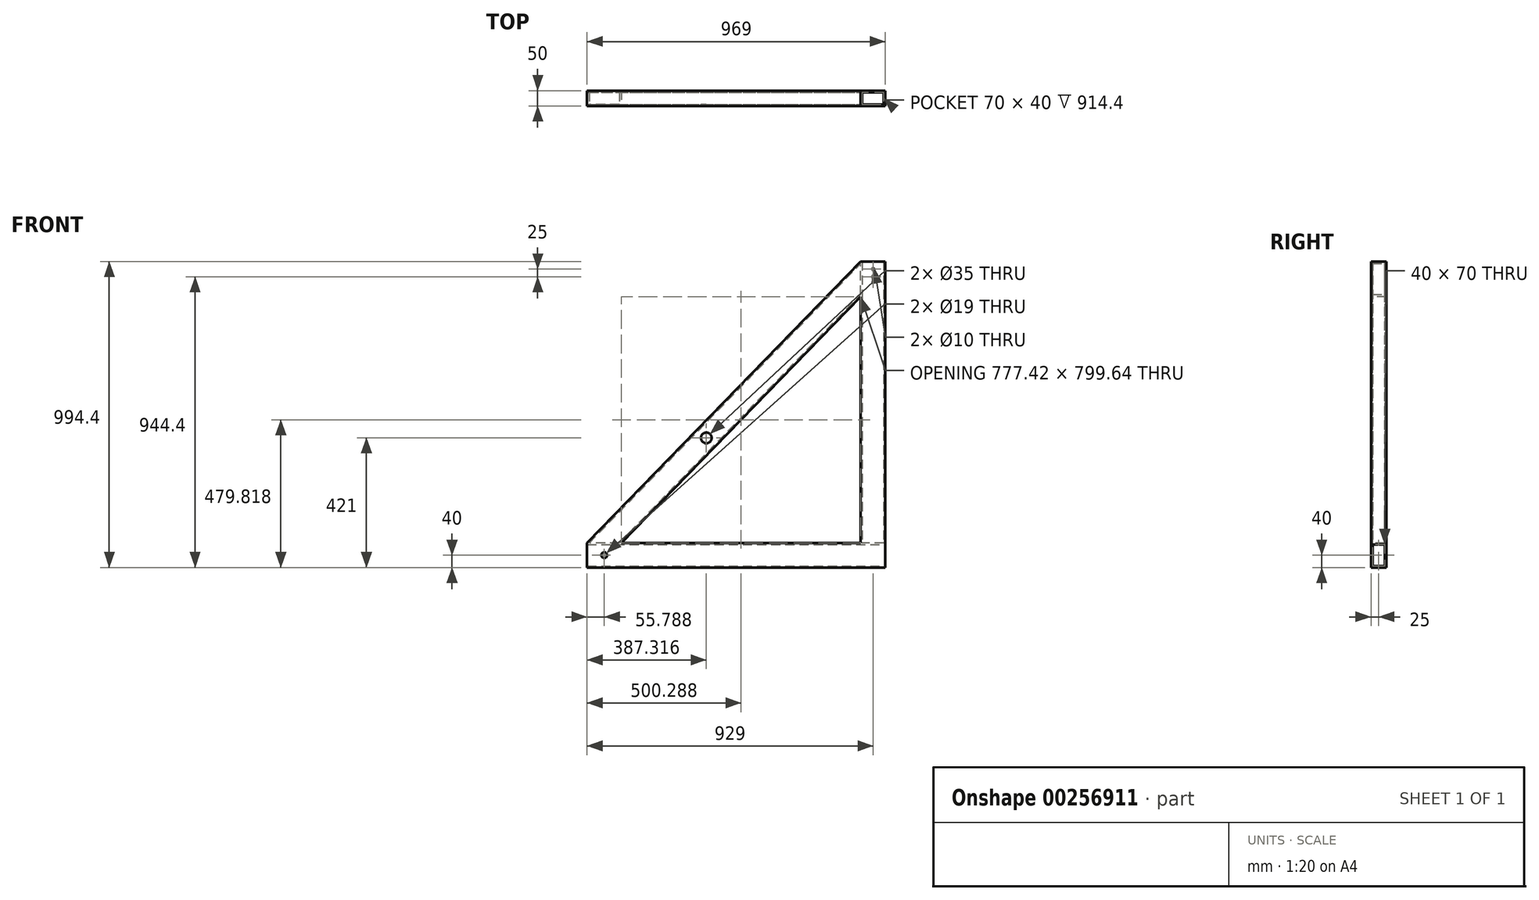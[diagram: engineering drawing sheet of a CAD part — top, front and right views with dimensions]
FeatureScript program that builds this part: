
annotation { "Feature Type Name" : "Feature", "Feature Type Description" : "" }
export const myFeature = defineFeature(function(context is Context, id is Id, definition is map)
    precondition{}
    {
        {
            var Q0;
            Q0=qCreatedBy(makeId("Right.planeOp"),FACE);
            var sketch = newSketch(context, id + "F0", { "sketchPlane" : qUnion([Q0])});
            skLineSegment(sketch, "E0.bottom", {"start": v(0, 0) * mm, "end": v(-50, 0) * mm});
            skLineSegment(sketch, "E0.top", {"start": v(0, 80) * mm, "end": v(-50, 80) * mm});
            skLineSegment(sketch, "E0.left", {"start": v(0, 0) * mm, "end": v(0, 80) * mm});
            skLineSegment(sketch, "E0.right", {"start": v(-50, 0) * mm, "end": v(-50, 80) * mm});
            skLineSegment(sketch, "E1.0", {"start": v(-5, 75) * mm, "end": v(-45, 75) * mm});
            skLineSegment(sketch, "E1.1", {"start": v(-5, 5) * mm, "end": v(-5, 75) * mm});
            skLineSegment(sketch, "E1.2", {"start": v(-5, 5) * mm, "end": v(-45, 5) * mm});
            skLineSegment(sketch, "E1.3", {"start": v(-45, 5) * mm, "end": v(-45, 75) * mm});
            skSolve(sketch);
        }
        {
            var Q0;
            Q0=makeQuery(id+"F0.imprint","IMPRINT",FACE,{"disambiguationData":[TD([[makeQuery(id+"F0.imprint","IMPRINT",EDGE,{"derivedFrom":sQuery(id+"F0.wireOp",EDGE,"E0.bottom")}),-1.0]])]});
            extrude(context, id + "F1", {"entities" : qUnion([Q0]), "oppositeDirection" : true, "depth" : 969 * mm});
        }
        {
            var Q0;
            Q0=makeQuery(id+"F1.opExtrude","SWEPT_FACE",FACE,{"disambiguationData":[OSD([sQuery(id+"F0.wireOp",EDGE,"E0.top")])]});
            var sketch = newSketch(context, id + "F2", { "sketchPlane" : qUnion([Q0])});
            skLineSegment(sketch, "E2.bottom", {"start": v(0, 0) * mm, "end": v(-80, 0) * mm});
            skLineSegment(sketch, "E2.top", {"start": v(0, -50) * mm, "end": v(-80, -50) * mm});
            skLineSegment(sketch, "E2.left", {"start": v(0, 0) * mm, "end": v(0, -50) * mm});
            skLineSegment(sketch, "E2.right", {"start": v(-80, 0) * mm, "end": v(-80, -50) * mm});
            skLineSegment(sketch, "E3.0", {"start": v(-5, -5) * mm, "end": v(-75, -5) * mm});
            skLineSegment(sketch, "E3.1", {"start": v(-5, -5) * mm, "end": v(-5, -45) * mm});
            skLineSegment(sketch, "E3.2", {"start": v(-5, -45) * mm, "end": v(-75, -45) * mm});
            skLineSegment(sketch, "E3.3", {"start": v(-75, -5) * mm, "end": v(-75, -45) * mm});
            skSolve(sketch);
        }
        {
            var Q0;
            Q0=makeQuery(id+"F2.imprint","IMPRINT",FACE,{"disambiguationData":[TD([[makeQuery(id+"F2.imprint","IMPRINT",EDGE,{"derivedFrom":sQuery(id+"F2.wireOp",EDGE,"E2.bottom")}),-1.0]])]});
            extrude(context, id + "F3", {"entities" : qUnion([Q0]), "operationType" : NewBodyOperationType.ADD, "depth" : 914.4 * mm});
        }
        {
            var Q0;
            Q0=makeQuery(id+"F3.boolean.opBoolean","MERGE",FACE,{"derivedFrom":[makeQuery(id+"F1.opExtrude","SWEPT_FACE",FACE,{"disambiguationData":[OSD([sQuery(id+"F0.wireOp",EDGE,"E0.right")])]}),makeQuery(id+"F3.opExtrude","SWEPT_FACE",FACE,{"disambiguationData":[OSD([sQuery(id+"F2.wireOp",EDGE,"E2.top")])]})]});
            var sketch = newSketch(context, id + "F4", { "sketchPlane" : qUnion([Q0])});
            skLineSegment(sketch, "E4", {"start": v(-969, 80) * mm, "end": v(-80, 994.4) * mm});
            skLineSegment(sketch, "E5.0", {"start": v(-857.42, 80) * mm, "end": v(-80, 879.64) * mm});
            skLineSegment(sketch, "E6", {"start": v(-80, 994.4) * mm, "end": v(-80, 879.64) * mm});
            skLineSegment(sketch, "E7", {"start": v(-969, 80) * mm, "end": v(-857.42, 80) * mm});
            skSolve(sketch);
        }
        {
            var Q0;
            Q0=makeQuery(id+"F4.imprint","IMPRINT",FACE,{"disambiguationData":[TD([[makeQuery(id+"F4.imprint","IMPRINT",EDGE,{"derivedFrom":sQuery(id+"F4.wireOp",EDGE,"E4")}),-1.0]])]});
            extrude(context, id + "F5", {"entities" : qUnion([Q0]), "operationType" : NewBodyOperationType.ADD, "oppositeDirection" : true, "depth" : 50 * mm});
        }
        {
            var Q0;
            Q0=makeQuery(id+"F5.boolean.opBoolean","MERGE",FACE,{"derivedFrom":[makeQuery(id+"F3.boolean.opBoolean","MERGE",FACE,{"derivedFrom":[makeQuery(id+"F1.opExtrude","SWEPT_FACE",FACE,{"disambiguationData":[OSD([sQuery(id+"F0.wireOp",EDGE,"E0.right")])]}),makeQuery(id+"F3.opExtrude","SWEPT_FACE",FACE,{"disambiguationData":[OSD([sQuery(id+"F2.wireOp",EDGE,"E2.top")])]})]}),makeQuery(id+"F5.opExtrude","CAP_FACE",FACE,{"disambiguationData":[OSD([sQuery(id+"F4.wireOp",EDGE,"E4"),sQuery(id+"F4.wireOp",EDGE,"E5.0"),sQuery(id+"F4.wireOp",EDGE,"E6"),sQuery(id+"F4.wireOp",EDGE,"E7")])],"isStart":true})]});
            var sketch = newSketch(context, id + "F6", { "sketchPlane" : qUnion([Q0])});
            skCircle(sketch, "E8", {"center": v(-581.68, 421) * mm, "radius": 17.5 * mm});
            skLineSegment(sketch, "E9", {"start": v(-969, 40) * mm, "end": v(0, 40) * mm, "construction": true});
            skLineSegment(sketch, "E10", {"start": v(-40, 994.4) * mm, "end": v(-40, 0) * mm, "construction": true});
            skLineSegment(sketch, "E11.0", {"start": v(-952.1, 40) * mm, "end": v(-40, 978.16) * mm, "construction": true});
            skPoint(sketch, "E12", {"position": v(-40, 40) * mm});
            skLineSegment(sketch, "E13", {"start": v(-969, 80) * mm, "end": v(-857.42, 80) * mm, "construction": true});
            skCircle(sketch, "E14", {"center": v(-913.21, 40) * mm, "radius": 9.5 * mm});
            skPoint(sketch, "E14.centerSnap0", {"position": v(-913.21, 80) * mm});
            skCircle(sketch, "E15", {"center": v(-40, 969.4) * mm, "radius": 5 * mm});
            skCircle(sketch, "E16", {"center": v(-40, 944.4) * mm, "radius": 5 * mm});
            skSolve(sketch);
        }
        {
            var Q0;
            Q0=makeQuery(id+"F6.imprint","IMPRINT",FACE,{"disambiguationData":[TD([[makeQuery(id+"F6.imprint","IMPRINT",EDGE,{"derivedFrom":sQuery(id+"F6.wireOp",EDGE,"E8")}),1.0]])]});
            var Q1;
            Q1=makeQuery(id+"F6.imprint","IMPRINT",FACE,{"disambiguationData":[TD([[makeQuery(id+"F6.imprint","IMPRINT",EDGE,{"derivedFrom":sQuery(id+"F6.wireOp",EDGE,"E14")}),1.0]])]});
            extrude(context, id + "F7", {"entities" : qUnion([Q0, Q1]), "operationType" : NewBodyOperationType.REMOVE, "endBound" : BoundingType.THROUGH_ALL, "oppositeDirection" : true, "depth" : 25.4 * mm});
        }
        {
            var Q0;
            Q0=makeQuery(id+"F7.boolean.opBoolean","COPY",FACE,{"derivedFrom":makeQuery(id+"F7.opExtrude","SWEPT_FACE",FACE,{"disambiguationData":[OSD([sQuery(id+"F6.wireOp",EDGE,"E8")])]})});
            var Q1;
            Q1=makeQuery(id+"F1.opExtrude","SWEPT_BODY",BODY,{"disambiguationData":[OSD([sQuery(id+"F0.wireOp",EDGE,"E0.bottom"),sQuery(id+"F0.wireOp",EDGE,"E0.top"),sQuery(id+"F0.wireOp",EDGE,"E0.left"),sQuery(id+"F0.wireOp",EDGE,"E0.right"),sQuery(id+"F0.wireOp",EDGE,"E1.0"),sQuery(id+"F0.wireOp",EDGE,"E1.1"),sQuery(id+"F0.wireOp",EDGE,"E1.2"),sQuery(id+"F0.wireOp",EDGE,"E1.3")])]});
            shell(context, id + "F8", {"entities" : qUnion([Q0]), "parts" : qUnion([Q1]), "thickness" : 5 * mm});
        }
        {
            var Q0;
            Q0=makeQuery(id+"F6.imprint","IMPRINT",FACE,{"disambiguationData":[TD([[makeQuery(id+"F6.imprint","IMPRINT",EDGE,{"derivedFrom":sQuery(id+"F6.wireOp",EDGE,"E15")}),1.0]])]});
            var Q1;
            Q1=makeQuery(id+"F6.imprint","IMPRINT",FACE,{"disambiguationData":[TD([[makeQuery(id+"F6.imprint","IMPRINT",EDGE,{"derivedFrom":sQuery(id+"F6.wireOp",EDGE,"E16")}),1.0]])]});
            extrude(context, id + "F9", {"entities" : qUnion([Q0, Q1]), "operationType" : NewBodyOperationType.REMOVE, "oppositeDirection" : true, "depth" : 52.83 * mm, "hasSecondDirection" : true, "secondDirectionOppositeDirection" : true, "secondDirectionDepth" : 25.4 * mm});
        }
    });
